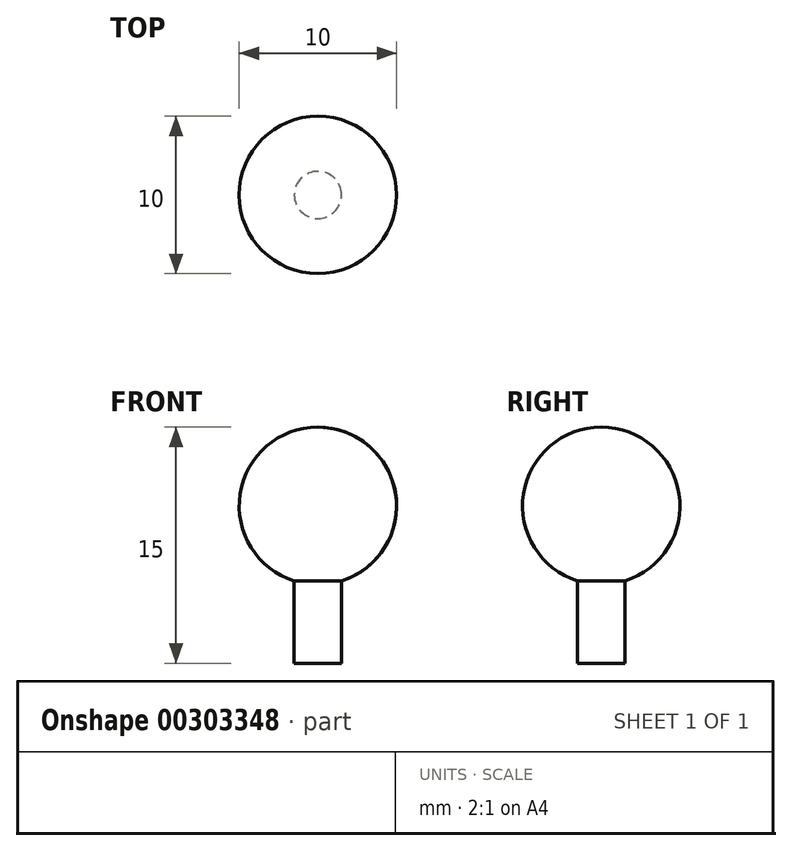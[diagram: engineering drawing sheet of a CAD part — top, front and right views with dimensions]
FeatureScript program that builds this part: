
annotation { "Feature Type Name" : "Feature", "Feature Type Description" : "" }
export const myFeature = defineFeature(function(context is Context, id is Id, definition is map)
    precondition{}
    {
        {
            var Q0;
            Q0=qCreatedBy(makeId("Front.planeOp"),FACE);
            var sketch = newSketch(context, id + "F0", { "sketchPlane" : qUnion([Q0])});
            skArc(sketch, "E0", {"start": v(1.5, -4.77) * mm, "mid": v(4.94, 0.76) * mm, "end": v(0, 5) * mm});
            skLineSegment(sketch, "E1.top", {"start": v(0, -10) * mm, "end": v(1.5, -10) * mm});
            skLineSegment(sketch, "E1.right", {"start": v(1.5, -4.77) * mm, "end": v(1.5, -10) * mm});
            skPoint(sketch, "E2.orphan", {"position": v(-1.5, 0) * mm});
            skLineSegment(sketch, "E3", {"start": v(0, 5) * mm, "end": v(0, -10) * mm});
            skPoint(sketch, "E4.orphan", {"position": v(-1.5, -10) * mm});
            skSolve(sketch);
        }
        {
            var Q0;
            Q0 = qSketchRegion(id + "F0", true);
            var Q1;
            Q1=sQuery(id+"F0.wireOp",EDGE,"E3");
            revolve(context, id + "F1", {"entities" : qUnion([Q0]), "axis" : qUnion([Q1]), "revolveType" : RevolveType.FULL});
        }
    });
